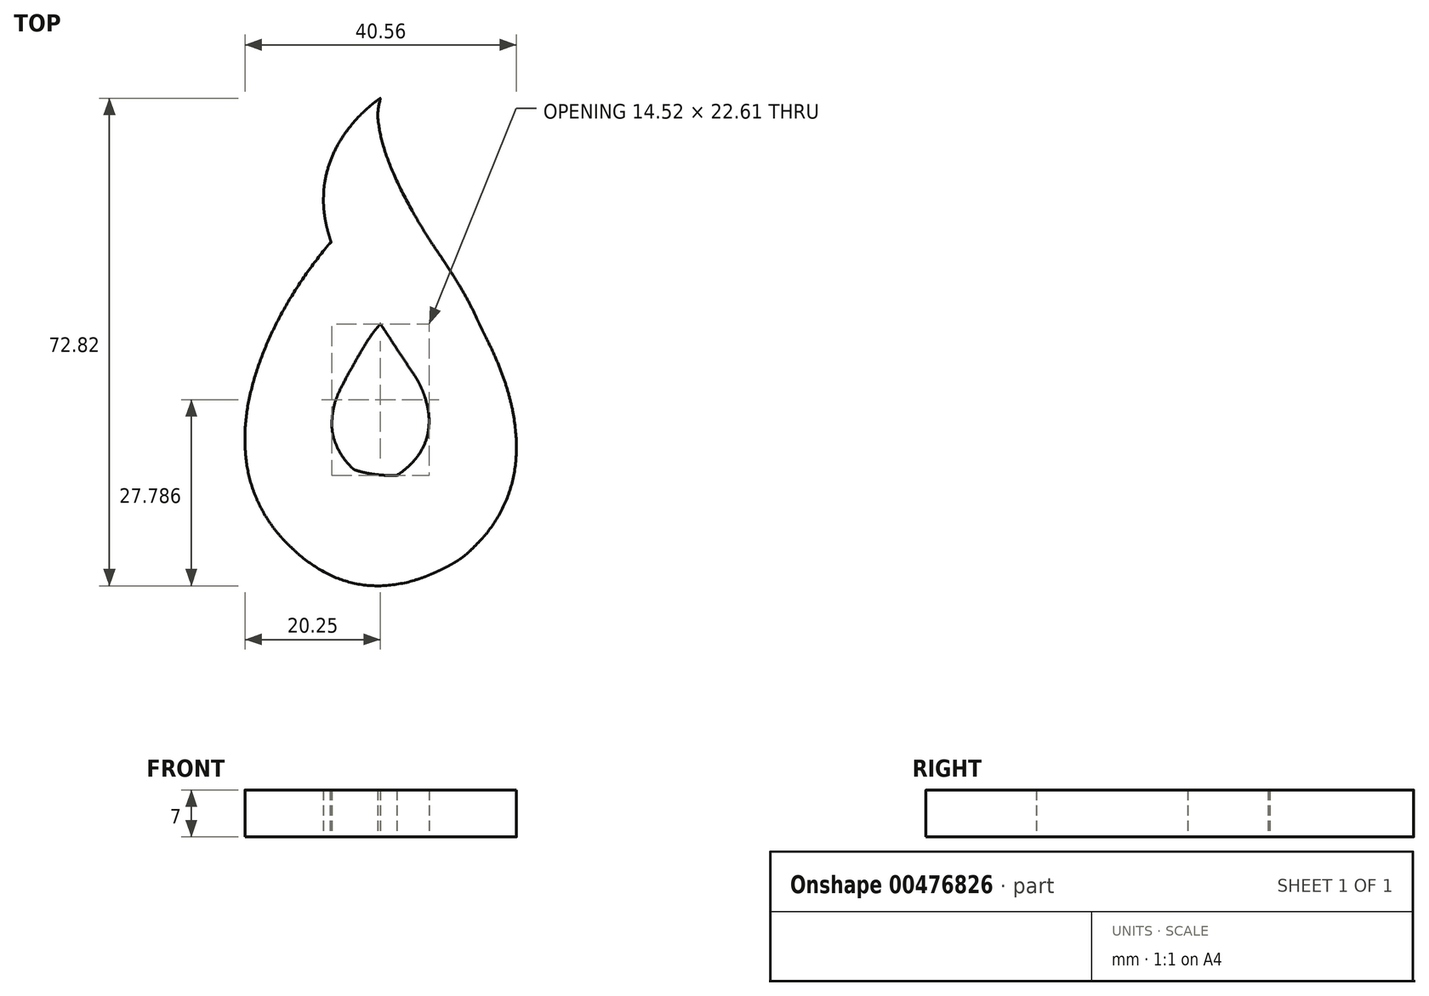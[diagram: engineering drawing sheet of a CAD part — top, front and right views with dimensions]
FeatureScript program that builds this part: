
annotation { "Feature Type Name" : "Feature", "Feature Type Description" : "" }
export const myFeature = defineFeature(function(context is Context, id is Id, definition is map)
    precondition{}
    {
        {
            var Q0;
            Q0=qCreatedBy(makeId("Top.planeOp"),FACE);
            var sketch = newSketch(context, id + "F0", { "sketchPlane" : qUnion([Q0])});
            skArc(sketch, "E0", {"start": v(-0.66, 35.99) * mm, "mid": v(-0.98, 35.74) * mm, "end": v(-1.3, 35.5) * mm});
            skArc(sketch, "E1", {"start": v(-1.3, 35.5) * mm, "mid": v(-1.59, 35.25) * mm, "end": v(-1.87, 35) * mm});
            skArc(sketch, "E2", {"start": v(-1.87, 35) * mm, "mid": v(-2.17, 34.73) * mm, "end": v(-2.46, 34.46) * mm});
            skArc(sketch, "E3", {"start": v(-2.46, 34.46) * mm, "mid": v(-2.8, 34.13) * mm, "end": v(-3.13, 33.79) * mm});
            skArc(sketch, "E4", {"start": v(-3.13, 33.79) * mm, "mid": v(-4.16, 32.67) * mm, "end": v(-5.1, 31.47) * mm});
            skArc(sketch, "E5", {"start": v(-5.1, 31.47) * mm, "mid": v(-5.92, 30.27) * mm, "end": v(-6.64, 29) * mm});
            skArc(sketch, "E6", {"start": v(-6.64, 29) * mm, "mid": v(-7.24, 27.72) * mm, "end": v(-7.74, 26.4) * mm});
            skArc(sketch, "E7", {"start": v(-7.74, 26.4) * mm, "mid": v(-8.12, 25.03) * mm, "end": v(-8.4, 23.63) * mm});
            skArc(sketch, "E8", {"start": v(-8.4, 23.63) * mm, "mid": v(-8.45, 23.24) * mm, "end": v(-8.48, 22.84) * mm});
            skArc(sketch, "E9", {"start": v(-8.48, 22.84) * mm, "mid": v(-8.5, 22.32) * mm, "end": v(-8.53, 21.8) * mm});
            skArc(sketch, "E10", {"start": v(-8.53, 21.8) * mm, "mid": v(-8.54, 21.27) * mm, "end": v(-8.53, 20.75) * mm});
            skArc(sketch, "E11", {"start": v(-8.53, 20.75) * mm, "mid": v(-8.52, 20.32) * mm, "end": v(-8.5, 19.9) * mm});
            skArc(sketch, "E12", {"start": v(-8.5, 19.9) * mm, "mid": v(-8.44, 19.36) * mm, "end": v(-8.37, 18.83) * mm});
            skArc(sketch, "E13", {"start": v(-8.37, 18.83) * mm, "mid": v(-8.28, 18.3) * mm, "end": v(-8.18, 17.76) * mm});
            skArc(sketch, "E14", {"start": v(-8.18, 17.76) * mm, "mid": v(-8.06, 17.22) * mm, "end": v(-7.92, 16.68) * mm});
            skArc(sketch, "E15", {"start": v(-7.92, 16.68) * mm, "mid": v(-7.77, 16.1) * mm, "end": v(-7.6, 15.54) * mm});
            skArc(sketch, "E16", {"start": v(-7.6, 15.54) * mm, "mid": v(-7.53, 15.33) * mm, "end": v(-7.47, 15.11) * mm});
            skArc(sketch, "E17", {"start": v(-7.47, 15.11) * mm, "mid": v(-7.44, 15.02) * mm, "end": v(-7.43, 14.94) * mm});
            skArc(sketch, "E18", {"start": v(-7.43, 14.94) * mm, "mid": v(-7.43, 14.88) * mm, "end": v(-7.43, 14.83) * mm});
            skArc(sketch, "E19", {"start": v(-7.43, 14.83) * mm, "mid": v(-7.45, 14.79) * mm, "end": v(-7.49, 14.75) * mm});
            skArc(sketch, "E20", {"start": v(-7.49, 14.75) * mm, "mid": v(-7.52, 14.72) * mm, "end": v(-7.56, 14.69) * mm});
            skArc(sketch, "E21", {"start": v(-7.56, 14.69) * mm, "mid": v(-7.56, 14.69) * mm, "end": v(-7.56, 14.69) * mm});
            skArc(sketch, "E22", {"start": v(-7.56, 14.69) * mm, "mid": v(-7.56, 14.69) * mm, "end": v(-7.56, 14.7) * mm});
            skArc(sketch, "E23", {"start": v(-7.56, 14.7) * mm, "mid": v(-7.54, 14.73) * mm, "end": v(-7.5, 14.76) * mm});
            skArc(sketch, "E24", {"start": v(-7.5, 14.76) * mm, "mid": v(-7.5, 14.79) * mm, "end": v(-7.48, 14.8) * mm});
            skArc(sketch, "E25", {"start": v(-7.48, 14.8) * mm, "mid": v(-7.47, 14.83) * mm, "end": v(-7.46, 14.85) * mm});
            skArc(sketch, "E26", {"start": v(-7.46, 14.85) * mm, "mid": v(-7.45, 14.87) * mm, "end": v(-7.45, 14.88) * mm});
            skArc(sketch, "E27", {"start": v(-7.45, 14.88) * mm, "mid": v(-7.45, 14.9) * mm, "end": v(-7.46, 14.9) * mm});
            skArc(sketch, "E28", {"start": v(-7.46, 14.9) * mm, "mid": v(-7.47, 14.9) * mm, "end": v(-7.48, 14.9) * mm});
            skArc(sketch, "E29", {"start": v(-7.48, 14.9) * mm, "mid": v(-7.61, 14.74) * mm, "end": v(-7.75, 14.59) * mm});
            skArc(sketch, "E30", {"start": v(-7.75, 14.59) * mm, "mid": v(-7.9, 14.4) * mm, "end": v(-8.05, 14.22) * mm});
            skArc(sketch, "E31", {"start": v(-8.05, 14.22) * mm, "mid": v(-8.23, 14) * mm, "end": v(-8.4, 13.78) * mm});
            skArc(sketch, "E32", {"start": v(-8.4, 13.78) * mm, "mid": v(-10.08, 11.6) * mm, "end": v(-11.68, 9.36) * mm});
            skArc(sketch, "E33", {"start": v(-11.68, 9.36) * mm, "mid": v(-13.1, 7.18) * mm, "end": v(-14.43, 4.93) * mm});
            skArc(sketch, "E34", {"start": v(-14.43, 4.93) * mm, "mid": v(-15.6, 2.72) * mm, "end": v(-16.68, 0.45) * mm});
            skArc(sketch, "E35", {"start": v(-16.68, 0.45) * mm, "mid": v(-17.63, -1.81) * mm, "end": v(-18.46, -4.12) * mm});
            skArc(sketch, "E36", {"start": v(-18.46, -4.12) * mm, "mid": v(-19.17, -6.52) * mm, "end": v(-19.73, -8.97) * mm});
            skArc(sketch, "E37", {"start": v(-19.73, -8.97) * mm, "mid": v(-20.09, -11.27) * mm, "end": v(-20.26, -13.6) * mm});
            skArc(sketch, "E38", {"start": v(-20.26, -13.6) * mm, "mid": v(-20.25, -15.77) * mm, "end": v(-20.04, -17.95) * mm});
            skArc(sketch, "E39", {"start": v(-20.04, -17.95) * mm, "mid": v(-19.66, -19.99) * mm, "end": v(-19.08, -21.98) * mm});
            skArc(sketch, "E40", {"start": v(-19.08, -21.98) * mm, "mid": v(-18.74, -22.91) * mm, "end": v(-18.34, -23.83) * mm});
            skArc(sketch, "E41", {"start": v(-18.34, -23.83) * mm, "mid": v(-17.9, -24.72) * mm, "end": v(-17.42, -25.6) * mm});
            skArc(sketch, "E42", {"start": v(-17.42, -25.6) * mm, "mid": v(-16.9, -26.46) * mm, "end": v(-16.33, -27.3) * mm});
            skArc(sketch, "E43", {"start": v(-16.33, -27.3) * mm, "mid": v(-15.72, -28.11) * mm, "end": v(-15.07, -28.9) * mm});
            skArc(sketch, "E44", {"start": v(-15.07, -28.9) * mm, "mid": v(-14.8, -29.2) * mm, "end": v(-14.53, -29.5) * mm});
            skArc(sketch, "E45", {"start": v(-14.53, -29.5) * mm, "mid": v(-14.14, -29.9) * mm, "end": v(-13.75, -30.29) * mm});
            skArc(sketch, "E46", {"start": v(-13.75, -30.29) * mm, "mid": v(-13.34, -30.69) * mm, "end": v(-12.92, -31.08) * mm});
            skArc(sketch, "E47", {"start": v(-12.92, -31.08) * mm, "mid": v(-12.58, -31.4) * mm, "end": v(-12.23, -31.7) * mm});
            skArc(sketch, "E48", {"start": v(-12.23, -31.7) * mm, "mid": v(-10.29, -33.2) * mm, "end": v(-8.2, -34.47) * mm});
            skArc(sketch, "E49", {"start": v(-8.2, -34.47) * mm, "mid": v(-6.1, -35.4) * mm, "end": v(-3.9, -36.04) * mm});
            skArc(sketch, "E50", {"start": v(-3.9, -36.04) * mm, "mid": v(-1.67, -36.37) * mm, "end": v(0.6, -36.38) * mm});
            skArc(sketch, "E51", {"start": v(0.6, -36.38) * mm, "mid": v(2.97, -36.08) * mm, "end": v(5.3, -35.51) * mm});
            skArc(sketch, "E52", {"start": v(5.3, -35.51) * mm, "mid": v(5.86, -35.33) * mm, "end": v(6.42, -35.13) * mm});
            skArc(sketch, "E53", {"start": v(6.42, -35.13) * mm, "mid": v(7.01, -34.9) * mm, "end": v(7.6, -34.65) * mm});
            skArc(sketch, "E54", {"start": v(7.6, -34.65) * mm, "mid": v(8.22, -34.38) * mm, "end": v(8.82, -34.1) * mm});
            skArc(sketch, "E55", {"start": v(8.82, -34.1) * mm, "mid": v(9.43, -33.8) * mm, "end": v(10.03, -33.48) * mm});
            skArc(sketch, "E56", {"start": v(10.03, -33.48) * mm, "mid": v(10.49, -33.24) * mm, "end": v(10.94, -32.99) * mm});
            skArc(sketch, "E57", {"start": v(10.94, -32.99) * mm, "mid": v(11.27, -32.8) * mm, "end": v(11.6, -32.58) * mm});
            skArc(sketch, "E58", {"start": v(11.6, -32.58) * mm, "mid": v(11.88, -32.4) * mm, "end": v(12.16, -32.2) * mm});
            skArc(sketch, "E59", {"start": v(12.16, -32.2) * mm, "mid": v(12.43, -31.99) * mm, "end": v(12.7, -31.76) * mm});
            skArc(sketch, "E60", {"start": v(12.7, -31.76) * mm, "mid": v(13.07, -31.44) * mm, "end": v(13.44, -31.1) * mm});
            skArc(sketch, "E61", {"start": v(13.44, -31.1) * mm, "mid": v(13.89, -30.66) * mm, "end": v(14.33, -30.21) * mm});
            skArc(sketch, "E62", {"start": v(14.33, -30.21) * mm, "mid": v(14.76, -29.76) * mm, "end": v(15.18, -29.31) * mm});
            skArc(sketch, "E63", {"start": v(15.18, -29.31) * mm, "mid": v(15.5, -28.96) * mm, "end": v(15.8, -28.6) * mm});
            skArc(sketch, "E64", {"start": v(15.8, -28.6) * mm, "mid": v(17.17, -26.66) * mm, "end": v(18.32, -24.58) * mm});
            skArc(sketch, "E65", {"start": v(18.32, -24.58) * mm, "mid": v(19.2, -22.43) * mm, "end": v(19.82, -20.19) * mm});
            skArc(sketch, "E66", {"start": v(19.82, -20.19) * mm, "mid": v(20.19, -17.8) * mm, "end": v(20.27, -15.4) * mm});
            skArc(sketch, "E67", {"start": v(20.27, -15.4) * mm, "mid": v(20.1, -12.78) * mm, "end": v(19.7, -10.19) * mm});
            skArc(sketch, "E68", {"start": v(19.7, -10.19) * mm, "mid": v(19.4, -8.87) * mm, "end": v(19.06, -7.57) * mm});
            skArc(sketch, "E69", {"start": v(19.06, -7.57) * mm, "mid": v(18.65, -6.24) * mm, "end": v(18.2, -4.92) * mm});
            skArc(sketch, "E70", {"start": v(18.2, -4.92) * mm, "mid": v(17.65, -3.53) * mm, "end": v(17.07, -2.15) * mm});
            skArc(sketch, "E71", {"start": v(17.07, -2.15) * mm, "mid": v(16.38, -0.65) * mm, "end": v(15.65, 0.84) * mm});
            skArc(sketch, "E72", {"start": v(15.65, 0.84) * mm, "mid": v(15.5, 1.16) * mm, "end": v(15.34, 1.47) * mm});
            skArc(sketch, "E73", {"start": v(15.34, 1.47) * mm, "mid": v(15.16, 1.83) * mm, "end": v(15, 2.18) * mm});
            skArc(sketch, "E74", {"start": v(15, 2.18) * mm, "mid": v(14.83, 2.52) * mm, "end": v(14.67, 2.86) * mm});
            skArc(sketch, "E75", {"start": v(14.67, 2.86) * mm, "mid": v(14.55, 3.12) * mm, "end": v(14.43, 3.38) * mm});
            skArc(sketch, "E76", {"start": v(14.43, 3.38) * mm, "mid": v(13.9, 4.5) * mm, "end": v(13.35, 5.6) * mm});
            skArc(sketch, "E77", {"start": v(13.35, 5.6) * mm, "mid": v(12.73, 6.75) * mm, "end": v(12.08, 7.9) * mm});
            skArc(sketch, "E78", {"start": v(12.08, 7.9) * mm, "mid": v(11.33, 9.14) * mm, "end": v(10.56, 10.38) * mm});
            skArc(sketch, "E79", {"start": v(10.56, 10.38) * mm, "mid": v(9.65, 11.77) * mm, "end": v(8.72, 13.15) * mm});
            skArc(sketch, "E80", {"start": v(8.72, 13.15) * mm, "mid": v(8.15, 14) * mm, "end": v(7.58, 14.87) * mm});
            skArc(sketch, "E81", {"start": v(7.58, 14.87) * mm, "mid": v(7.07, 15.66) * mm, "end": v(6.56, 16.46) * mm});
            skArc(sketch, "E82", {"start": v(6.56, 16.46) * mm, "mid": v(6.09, 17.23) * mm, "end": v(5.62, 18.02) * mm});
            skArc(sketch, "E83", {"start": v(5.62, 18.02) * mm, "mid": v(5.15, 18.83) * mm, "end": v(4.7, 19.64) * mm});
            skArc(sketch, "E84", {"start": v(4.7, 19.64) * mm, "mid": v(3.34, 22.19) * mm, "end": v(2.08, 24.8) * mm});
            skArc(sketch, "E85", {"start": v(2.08, 24.8) * mm, "mid": v(1.17, 27.01) * mm, "end": v(0.4, 29.29) * mm});
            skArc(sketch, "E86", {"start": v(0.4, 29.29) * mm, "mid": v(-0.07, 31.16) * mm, "end": v(-0.37, 33.06) * mm});
            skArc(sketch, "E87", {"start": v(-0.37, 33.06) * mm, "mid": v(-0.4, 34.51) * mm, "end": v(-0.15, 35.95) * mm});
            skArc(sketch, "E88", {"start": v(-0.15, 35.95) * mm, "mid": v(-0.13, 36.03) * mm, "end": v(-0.1, 36.12) * mm});
            skArc(sketch, "E89", {"start": v(-0.1, 36.12) * mm, "mid": v(-0.09, 36.2) * mm, "end": v(-0.07, 36.27) * mm});
            skArc(sketch, "E90", {"start": v(-0.07, 36.27) * mm, "mid": v(-0.06, 36.33) * mm, "end": v(-0.04, 36.4) * mm});
            skArc(sketch, "E91", {"start": v(-0.04, 36.4) * mm, "mid": v(-0.04, 36.4) * mm, "end": v(-0.05, 36.41) * mm});
            skArc(sketch, "E92", {"start": v(-0.05, 36.41) * mm, "mid": v(-0.06, 36.41) * mm, "end": v(-0.07, 36.41) * mm});
            skArc(sketch, "E93", {"start": v(-0.07, 36.41) * mm, "mid": v(-0.15, 36.35) * mm, "end": v(-0.24, 36.3) * mm});
            skArc(sketch, "E94", {"start": v(-0.24, 36.3) * mm, "mid": v(-0.33, 36.23) * mm, "end": v(-0.43, 36.16) * mm});
            skArc(sketch, "E95", {"start": v(-0.43, 36.16) * mm, "mid": v(-0.54, 36.07) * mm, "end": v(-0.66, 35.99) * mm});
            skArc(sketch, "E96", {"start": v(1.29, 0.7) * mm, "mid": v(1.72, 0.04) * mm, "end": v(2.15, -0.62) * mm});
            skArc(sketch, "E97", {"start": v(2.15, -0.62) * mm, "mid": v(2.63, -1.34) * mm, "end": v(3.1, -2.07) * mm});
            skArc(sketch, "E98", {"start": v(3.1, -2.07) * mm, "mid": v(3.6, -2.82) * mm, "end": v(4.1, -3.57) * mm});
            skArc(sketch, "E99", {"start": v(4.1, -3.57) * mm, "mid": v(4.59, -4.29) * mm, "end": v(5.07, -5) * mm});
            skArc(sketch, "E100", {"start": v(5.07, -5) * mm, "mid": v(5.3, -5.36) * mm, "end": v(5.5, -5.71) * mm});
            skArc(sketch, "E101", {"start": v(5.5, -5.71) * mm, "mid": v(5.72, -6.1) * mm, "end": v(5.92, -6.5) * mm});
            skArc(sketch, "E102", {"start": v(5.92, -6.5) * mm, "mid": v(6.11, -6.93) * mm, "end": v(6.3, -7.36) * mm});
            skArc(sketch, "E103", {"start": v(6.3, -7.36) * mm, "mid": v(6.46, -7.8) * mm, "end": v(6.62, -8.26) * mm});
            skArc(sketch, "E104", {"start": v(6.62, -8.26) * mm, "mid": v(6.94, -9.44) * mm, "end": v(7.16, -10.64) * mm});
            skArc(sketch, "E105", {"start": v(7.16, -10.64) * mm, "mid": v(7.23, -11.77) * mm, "end": v(7.17, -12.9) * mm});
            skArc(sketch, "E106", {"start": v(7.17, -12.9) * mm, "mid": v(6.97, -13.98) * mm, "end": v(6.64, -15.01) * mm});
            skArc(sketch, "E107", {"start": v(6.64, -15.01) * mm, "mid": v(6.18, -16.02) * mm, "end": v(5.6, -16.95) * mm});
            skArc(sketch, "E108", {"start": v(5.6, -16.95) * mm, "mid": v(5.32, -17.32) * mm, "end": v(5.03, -17.66) * mm});
            skArc(sketch, "E109", {"start": v(5.03, -17.66) * mm, "mid": v(4.67, -18.04) * mm, "end": v(4.3, -18.41) * mm});
            skArc(sketch, "E110", {"start": v(4.3, -18.41) * mm, "mid": v(3.9, -18.78) * mm, "end": v(3.5, -19.12) * mm});
            skArc(sketch, "E111", {"start": v(3.5, -19.12) * mm, "mid": v(3.12, -19.42) * mm, "end": v(2.73, -19.7) * mm});
            skLineSegment(sketch, "E112", {"start": v(2.73, -19.7) * mm, "end": v(2.39, -19.93) * mm});
            skLineSegment(sketch, "E113", {"start": v(2.39, -19.93) * mm, "end": v(1.57, -19.93) * mm});
            skArc(sketch, "E114", {"start": v(1.57, -19.93) * mm, "mid": v(0.98, -19.92) * mm, "end": v(0.38, -19.89) * mm});
            skArc(sketch, "E115", {"start": v(0.38, -19.89) * mm, "mid": v(-0.24, -19.83) * mm, "end": v(-0.86, -19.76) * mm});
            skArc(sketch, "E116", {"start": v(-0.86, -19.76) * mm, "mid": v(-1.48, -19.67) * mm, "end": v(-2.08, -19.56) * mm});
            skArc(sketch, "E117", {"start": v(-2.08, -19.56) * mm, "mid": v(-2.65, -19.44) * mm, "end": v(-3.2, -19.3) * mm});
            skArc(sketch, "E118", {"start": v(-3.2, -19.3) * mm, "mid": v(-3.45, -19.23) * mm, "end": v(-3.7, -19.15) * mm});
            skArc(sketch, "E119", {"start": v(-3.7, -19.15) * mm, "mid": v(-3.8, -19.12) * mm, "end": v(-3.92, -19.06) * mm});
            skArc(sketch, "E120", {"start": v(-3.92, -19.06) * mm, "mid": v(-4, -19) * mm, "end": v(-4.1, -18.94) * mm});
            skArc(sketch, "E121", {"start": v(-4.1, -18.94) * mm, "mid": v(-4.23, -18.82) * mm, "end": v(-4.36, -18.7) * mm});
            skArc(sketch, "E122", {"start": v(-4.36, -18.7) * mm, "mid": v(-4.88, -18.14) * mm, "end": v(-5.37, -17.55) * mm});
            skArc(sketch, "E123", {"start": v(-5.37, -17.55) * mm, "mid": v(-5.8, -16.94) * mm, "end": v(-6.19, -16.3) * mm});
            skArc(sketch, "E124", {"start": v(-6.19, -16.3) * mm, "mid": v(-6.52, -15.65) * mm, "end": v(-6.8, -14.98) * mm});
            skArc(sketch, "E125", {"start": v(-6.8, -14.98) * mm, "mid": v(-7.01, -14.3) * mm, "end": v(-7.17, -13.62) * mm});
            skArc(sketch, "E126", {"start": v(-7.17, -13.62) * mm, "mid": v(-7.26, -12.97) * mm, "end": v(-7.29, -12.31) * mm});
            skArc(sketch, "E127", {"start": v(-7.29, -12.31) * mm, "mid": v(-7.26, -11.56) * mm, "end": v(-7.19, -10.81) * mm});
            skArc(sketch, "E128", {"start": v(-7.19, -10.81) * mm, "mid": v(-7.06, -10.05) * mm, "end": v(-6.9, -9.3) * mm});
            skArc(sketch, "E129", {"start": v(-6.9, -9.3) * mm, "mid": v(-6.68, -8.6) * mm, "end": v(-6.43, -7.92) * mm});
            skArc(sketch, "E130", {"start": v(-6.43, -7.92) * mm, "mid": v(-6, -7) * mm, "end": v(-5.55, -6.1) * mm});
            skArc(sketch, "E131", {"start": v(-5.55, -6.1) * mm, "mid": v(-4.79, -4.7) * mm, "end": v(-4.02, -3.3) * mm});
            skArc(sketch, "E132", {"start": v(-4.02, -3.3) * mm, "mid": v(-3.23, -1.92) * mm, "end": v(-2.42, -0.55) * mm});
            skArc(sketch, "E133", {"start": v(-2.42, -0.55) * mm, "mid": v(-1.88, 0.31) * mm, "end": v(-1.3, 1.16) * mm});
            skArc(sketch, "E134", {"start": v(-1.3, 1.16) * mm, "mid": v(-1.13, 1.39) * mm, "end": v(-0.96, 1.62) * mm});
            skArc(sketch, "E135", {"start": v(-0.96, 1.62) * mm, "mid": v(-0.75, 1.88) * mm, "end": v(-0.54, 2.13) * mm});
            skArc(sketch, "E136", {"start": v(-0.54, 2.13) * mm, "mid": v(-0.32, 2.39) * mm, "end": v(-0.1, 2.64) * mm});
            skArc(sketch, "E137", {"start": v(-0.1, 2.64) * mm, "mid": v(-0.07, 2.67) * mm, "end": v(-0.03, 2.68) * mm});
            skArc(sketch, "E138", {"start": v(-0.03, 2.68) * mm, "mid": v(-0.02, 2.68) * mm, "end": v(0, 2.66) * mm});
            skArc(sketch, "E139", {"start": v(0, 2.66) * mm, "mid": v(0.18, 2.38) * mm, "end": v(0.37, 2.1) * mm});
            skArc(sketch, "E140", {"start": v(0.37, 2.1) * mm, "mid": v(0.58, 1.78) * mm, "end": v(0.8, 1.46) * mm});
            skArc(sketch, "E141", {"start": v(0.8, 1.46) * mm, "mid": v(1.04, 1.08) * mm, "end": v(1.29, 0.7) * mm});
            skSolve(sketch);
        }
        {
            var Q0;
            Q0=makeQuery(id+"F0.imprint","IMPRINT",FACE,{"disambiguationData":[TD([[makeQuery(id+"F0.imprint","IMPRINT",EDGE,{"derivedFrom":sQuery(id+"F0.wireOp",EDGE,"E0")}),1.0]])]});
            extrude(context, id + "F1", {"entities" : qUnion([Q0]), "depth" : 7 * mm});
        }
    });
